FCSTD DOCUMENT  (FreeCAD 0.17R11204 (Git))
Label: Flow1D_thermomech
License: All rights reserved
LicenseURL: http://en.wikipedia.org/wiki/All_rights_reserved
objects: Fem::FeaturePython×12, Part::Part2DObjectPython×1, Fem::FemSolverObjectPython×1, Fem::FemMeshObjectPython×1, App::MaterialObjectPython×1, Fem::FemResultObjectPython×1, Fem::FemAnalysisPython×1
note: 1 computed .brp shape members not serialized (recipe doc carries the construction recipe); baked Part::Feature solids carry a one-line shape summary decoded from their .brp

FEATURE [Part::Part2DObjectPython] DWire  # Draft 2D object (typed FeaturePython)
  ChamferSize = 0
  Closed = false
  End = (15047,-2e-12,-7847.97)
  FilletRadius = 0
  Length = 30059.3
  MakeFace = false
  Placement = pos=(0,0,0) rot=(1,0,0;1.5708rad)
  Points = (14) [(0,50,0),(0,-50,0),(0,-4300,0),(4950,-4300,0),(5000,-4300,0),(8535.53,-7835.53,0),(8569.88,-7870.88,0),(12105.4,-11406.4,0),(12140.8,-11441.8,0),+5 more]
  Start = (0,0,50)
  Subdivisions = 0
FEATURE [Fem::FemSolverObjectPython] CalculiX  # FEM object (typed FeaturePython)
  AnalysisType = 2
  EigenmodeHighLimit = 1000000
  EigenmodeLowLimit = 0
  EigenmodesCount = 10
  GeometricalNonlinearity = 0
  IterationsControlParameterCutb = 0.25,0.5,0.75,0.85,,,1.5,
  IterationsControlParameterIter = 4,8,9,200,10,400,,200,,
  IterationsControlParameterTimeUse = false
  IterationsThermoMechMaximum = 2000
  IterationsUserDefinedIncrementations = false
  IterationsUserDefinedTimeStepLength = 0.1, 1.0
  MaterialNonlinearity = 0
  MatrixSolverType = 0
  SolverType = FemSolverCalculix
  SplitInputWriter = false
  ThermoMechSteadyState = true
  TimeEnd = 1
  TimeInitialStep = 1
FEATURE [Fem::FemMeshObjectPython] DWire_Mesh  # FEM object (typed FeaturePython)
  Algorithm2D = 0
  Algorithm3D = 0
  CharacteristicLengthMax = 7000
  CharacteristicLengthMin = 7000
  ElementDimension = 1
  ElementOrder = 1
  HighOrderOptimize = false
  OptimizeNetgen = false
  OptimizeStd = true
  Part = -> DWire
  RecombineAll = false
FEATURE [App::MaterialObjectPython] FluidMaterial  # material (typed FeaturePython)
  Category = 1
  Material = Density=998.0 kg/m^3,Description=Standard distilled water properties at 20 Degrees Celsius and 1 atm,DynamicViscosity=1.003e-3 kg/m/s,+7 more (map truncated)
FEATURE [Fem::FeaturePython] FemConstraintSelfWeight  # FEM object (typed FeaturePython)
  Gravity_x = 0
  Gravity_y = 0
  Gravity_z = -1
FEATURE [Fem::FeaturePython] ElementFluid1D  # FEM object (typed FeaturePython)
  BendAngle = 0
  BendLossCoefficient = 0
  BendPipeArea = 20
  BendRadiusDiameter = 1
  ChannelSectionType = 0
  ColebrookeArea = 20
  ColebrookeFormFactor = 1
  ColebrookeGrainDiameter = 0.0025
  ColebrookeRadius = 1
  ContractArea1 = 20
  ContractArea2 = 10
  DiaphragmArea = 20
  DiaphragmPipeArea = 20
  EnlargeArea1 = 10
  EnlargeArea2 = 20
  EntranceArea = 20
  EntrancePipeArea = 20
  GasSectionType = 0
  GateValveClosingCoeff = 0.125
  GateValvePipeArea = 20
  InletFlowRate = 1
  InletFlowRateActive = false
  InletPressure = 0.1
  InletPressureActive = true
  LiquidSectionType = 3
  ManningArea = 10
  ManningCoefficient = 0.002
  ManningRadius = 1
  OutletFlowRate = 1
  OutletFlowRateActive = false
  OutletPressure = 1
  OutletPressureActive = true
  PumpFlowRate = [0,0.000104,0.000208,0.000313,0.000417]
  PumpHeadLoss = [30,29.17,26.67,23.33,18.33]
  References = -> [DWire]
  SectionType = 0
FEATURE [Fem::FeaturePython] ElementFluid1D001  # FEM object (typed FeaturePython)
  BendAngle = 0
  BendLossCoefficient = 0
  BendPipeArea = 20
  BendRadiusDiameter = 1
  ChannelSectionType = 0
  ColebrookeArea = 20
  ColebrookeFormFactor = 1
  ColebrookeGrainDiameter = 0.0025
  ColebrookeRadius = 1
  ContractArea1 = 20
  ContractArea2 = 10
  DiaphragmArea = 20
  DiaphragmPipeArea = 20
  EnlargeArea1 = 10
  EnlargeArea2 = 20
  EntranceArea = 25133
  EntrancePipeArea = 31416
  GasSectionType = 0
  GateValveClosingCoeff = 0.125
  GateValvePipeArea = 20
  InletFlowRate = 1
  InletFlowRateActive = false
  InletPressure = 1
  InletPressureActive = true
  LiquidSectionType = 5
  ManningArea = 10
  ManningCoefficient = 0.002
  ManningRadius = 1
  OutletFlowRate = 1
  OutletFlowRateActive = false
  OutletPressure = 1
  OutletPressureActive = true
  PumpFlowRate = [0,0.000104,0.000208,0.000313,0.000417]
  PumpHeadLoss = [30,29.17,26.67,23.33,18.33]
  References = -> [DWire]
  SectionType = 0
FEATURE [Fem::FeaturePython] ElementFluid1D002  # FEM object (typed FeaturePython)
  BendAngle = 0
  BendLossCoefficient = 0
  BendPipeArea = 20
  BendRadiusDiameter = 1
  ChannelSectionType = 0
  ColebrookeArea = 20
  ColebrookeFormFactor = 1
  ColebrookeGrainDiameter = 0.0025
  ColebrookeRadius = 1
  ContractArea1 = 20
  ContractArea2 = 10
  DiaphragmArea = 20
  DiaphragmPipeArea = 20
  EnlargeArea1 = 10
  EnlargeArea2 = 20
  EntranceArea = 20
  EntrancePipeArea = 20
  GasSectionType = 0
  GateValveClosingCoeff = 0.125
  GateValvePipeArea = 20
  InletFlowRate = 1
  InletFlowRateActive = false
  InletPressure = 1
  InletPressureActive = true
  LiquidSectionType = 0
  ManningArea = 31416
  ManningCoefficient = 0.002
  ManningRadius = 50
  OutletFlowRate = 1
  OutletFlowRateActive = false
  OutletPressure = 1
  OutletPressureActive = true
  PumpFlowRate = [0,0.000104,0.000208,0.000313,0.000417]
  PumpHeadLoss = [30,29.17,26.67,23.33,18.33]
  References = -> [DWire]
  SectionType = 0
FEATURE [Fem::FeaturePython] ElementFluid1D003  # FEM object (typed FeaturePython)
  BendAngle = 45
  BendLossCoefficient = 0.4
  BendPipeArea = 31416
  BendRadiusDiameter = 1.5
  ChannelSectionType = 0
  ColebrookeArea = 20
  ColebrookeFormFactor = 1
  ColebrookeGrainDiameter = 0.0025
  ColebrookeRadius = 1
  ContractArea1 = 20
  ContractArea2 = 10
  DiaphragmArea = 20
  DiaphragmPipeArea = 20
  EnlargeArea1 = 10
  EnlargeArea2 = 20
  EntranceArea = 20
  EntrancePipeArea = 20
  GasSectionType = 0
  GateValveClosingCoeff = 0.125
  GateValvePipeArea = 20
  InletFlowRate = 1
  InletFlowRateActive = false
  InletPressure = 1
  InletPressureActive = true
  LiquidSectionType = 7
  ManningArea = 10
  ManningCoefficient = 0.002
  ManningRadius = 1
  OutletFlowRate = 1
  OutletFlowRateActive = false
  OutletPressure = 1
  OutletPressureActive = true
  PumpFlowRate = [0,0.000104,0.000208,0.000313,0.000417]
  PumpHeadLoss = [30,29.17,26.67,23.33,18.33]
  References = -> [DWire]
  SectionType = 0
FEATURE [Fem::FeaturePython] ElementFluid1D004  # FEM object (typed FeaturePython)
  BendAngle = 0
  BendLossCoefficient = 0
  BendPipeArea = 20
  BendRadiusDiameter = 1
  ChannelSectionType = 0
  ColebrookeArea = 20
  ColebrookeFormFactor = 1
  ColebrookeGrainDiameter = 0.0025
  ColebrookeRadius = 1
  ContractArea1 = 20
  ContractArea2 = 10
  DiaphragmArea = 20
  DiaphragmPipeArea = 20
  EnlargeArea1 = 31416
  EnlargeArea2 = 70686
  EntranceArea = 20
  EntrancePipeArea = 20
  GasSectionType = 0
  GateValveClosingCoeff = 0.125
  GateValvePipeArea = 20
  InletFlowRate = 1
  InletFlowRateActive = false
  InletPressure = 1
  InletPressureActive = true
  LiquidSectionType = 1
  ManningArea = 10
  ManningCoefficient = 0.002
  ManningRadius = 1
  OutletFlowRate = 1
  OutletFlowRateActive = false
  OutletPressure = 1
  OutletPressureActive = true
  PumpFlowRate = [0,0.000104,0.000208,0.000313,0.000417]
  PumpHeadLoss = [30,29.17,26.67,23.33,18.33]
  References = -> [DWire]
  SectionType = 0
FEATURE [Fem::FeaturePython] ElementFluid1D005  # FEM object (typed FeaturePython)
  BendAngle = 0
  BendLossCoefficient = 0
  BendPipeArea = 20
  BendRadiusDiameter = 1
  ChannelSectionType = 0
  ColebrookeArea = 20
  ColebrookeFormFactor = 1
  ColebrookeGrainDiameter = 0.0025
  ColebrookeRadius = 1
  ContractArea1 = 20
  ContractArea2 = 10
  DiaphragmArea = 20
  DiaphragmPipeArea = 20
  EnlargeArea1 = 10
  EnlargeArea2 = 20
  EntranceArea = 20
  EntrancePipeArea = 20
  GasSectionType = 0
  GateValveClosingCoeff = 0.125
  GateValvePipeArea = 20
  InletFlowRate = 1
  InletFlowRateActive = false
  InletPressure = 1
  InletPressureActive = true
  LiquidSectionType = 0
  ManningArea = 70686
  ManningCoefficient = 0.002
  ManningRadius = 75
  OutletFlowRate = 1
  OutletFlowRateActive = false
  OutletPressure = 1
  OutletPressureActive = true
  PumpFlowRate = [0,0.000104,0.000208,0.000313,0.000417]
  PumpHeadLoss = [30,29.17,26.67,23.33,18.33]
  References = -> [DWire]
  SectionType = 0
FEATURE [Fem::FeaturePython] ElementFluid1D006  # FEM object (typed FeaturePython)
  BendAngle = 0
  BendLossCoefficient = 0
  BendPipeArea = 20
  BendRadiusDiameter = 1
  ChannelSectionType = 0
  ColebrookeArea = 20
  ColebrookeFormFactor = 1
  ColebrookeGrainDiameter = 0.0025
  ColebrookeRadius = 1
  ContractArea1 = 70686
  ContractArea2 = 17671
  DiaphragmArea = 20
  DiaphragmPipeArea = 20
  EnlargeArea1 = 10
  EnlargeArea2 = 20
  EntranceArea = 20
  EntrancePipeArea = 20
  GasSectionType = 0
  GateValveClosingCoeff = 0.125
  GateValvePipeArea = 20
  InletFlowRate = 1
  InletFlowRateActive = false
  InletPressure = 1
  InletPressureActive = true
  LiquidSectionType = 2
  ManningArea = 10
  ManningCoefficient = 0.002
  ManningRadius = 1
  OutletFlowRate = 1
  OutletFlowRateActive = false
  OutletPressure = 1
  OutletPressureActive = true
  PumpFlowRate = [0,0.000104,0.000208,0.000313,0.000417]
  PumpHeadLoss = [30,29.17,26.67,23.33,18.33]
  References = -> [DWire]
  SectionType = 0
FEATURE [Fem::FeaturePython] ElementFluid1D007  # FEM object (typed FeaturePython)
  BendAngle = 0
  BendLossCoefficient = 0
  BendPipeArea = 20
  BendRadiusDiameter = 1
  ChannelSectionType = 0
  ColebrookeArea = 20
  ColebrookeFormFactor = 1
  ColebrookeGrainDiameter = 0.0025
  ColebrookeRadius = 1
  ContractArea1 = 20
  ContractArea2 = 10
  DiaphragmArea = 20
  DiaphragmPipeArea = 20
  EnlargeArea1 = 10
  EnlargeArea2 = 20
  EntranceArea = 20
  EntrancePipeArea = 20
  GasSectionType = 0
  GateValveClosingCoeff = 0.125
  GateValvePipeArea = 20
  InletFlowRate = 1
  InletFlowRateActive = false
  InletPressure = 1
  InletPressureActive = true
  LiquidSectionType = 0
  ManningArea = 17671
  ManningCoefficient = 0.002
  ManningRadius = 37.5
  OutletFlowRate = 1
  OutletFlowRateActive = false
  OutletPressure = 1
  OutletPressureActive = true
  PumpFlowRate = [0,0.000104,0.000208,0.000313,0.000417]
  PumpHeadLoss = [30,29.17,26.67,23.33,18.33]
  References = -> [DWire]
  SectionType = 0
FEATURE [Fem::FeaturePython] ElementFluid1D008  # FEM object (typed FeaturePython)
  BendAngle = 0
  BendLossCoefficient = 0
  BendPipeArea = 20
  BendRadiusDiameter = 1
  ChannelSectionType = 0
  ColebrookeArea = 20
  ColebrookeFormFactor = 1
  ColebrookeGrainDiameter = 0.0025
  ColebrookeRadius = 1
  ContractArea1 = 20
  ContractArea2 = 10
  DiaphragmArea = 20
  DiaphragmPipeArea = 20
  EnlargeArea1 = 10
  EnlargeArea2 = 20
  EntranceArea = 20
  EntrancePipeArea = 20
  GasSectionType = 0
  GateValveClosingCoeff = 0.5
  GateValvePipeArea = 17661
  InletFlowRate = 1
  InletFlowRateActive = false
  InletPressure = 1
  InletPressureActive = true
  LiquidSectionType = 8
  ManningArea = 10
  ManningCoefficient = 0.002
  ManningRadius = 1
  OutletFlowRate = 1
  OutletFlowRateActive = false
  OutletPressure = 1
  OutletPressureActive = true
  PumpFlowRate = [0,0.000104,0.000208,0.000313,0.000417]
  PumpHeadLoss = [30,29.17,26.67,23.33,18.33]
  References = -> [DWire]
  SectionType = 0
FEATURE [Fem::FeaturePython] ElementFluid1D009  # FEM object (typed FeaturePython)
  BendAngle = 0
  BendLossCoefficient = 0
  BendPipeArea = 20
  BendRadiusDiameter = 1
  ChannelSectionType = 0
  ColebrookeArea = 20
  ColebrookeFormFactor = 1
  ColebrookeGrainDiameter = 0.0025
  ColebrookeRadius = 1
  ContractArea1 = 20
  ContractArea2 = 10
  DiaphragmArea = 20
  DiaphragmPipeArea = 20
  EnlargeArea1 = 17671
  EnlargeArea2 = 1000000000000
  EntranceArea = 20
  EntrancePipeArea = 20
  GasSectionType = 0
  GateValveClosingCoeff = 0.125
  GateValvePipeArea = 20
  InletFlowRate = 1
  InletFlowRateActive = false
  InletPressure = 1
  InletPressureActive = true
  LiquidSectionType = 1
  ManningArea = 10
  ManningCoefficient = 0.002
  ManningRadius = 1
  OutletFlowRate = 1
  OutletFlowRateActive = false
  OutletPressure = 1
  OutletPressureActive = true
  PumpFlowRate = [0,0.000104,0.000208,0.000313,0.000417]
  PumpHeadLoss = [30,29.17,26.67,23.33,18.33]
  References = -> [DWire]
  SectionType = 0
FEATURE [Fem::FeaturePython] ElementFluid1D010  # FEM object (typed FeaturePython)
  BendAngle = 0
  BendLossCoefficient = 0
  BendPipeArea = 20
  BendRadiusDiameter = 1
  ChannelSectionType = 0
  ColebrookeArea = 20
  ColebrookeFormFactor = 1
  ColebrookeGrainDiameter = 0.0025
  ColebrookeRadius = 1
  ContractArea1 = 20
  ContractArea2 = 10
  DiaphragmArea = 20
  DiaphragmPipeArea = 20
  EnlargeArea1 = 10
  EnlargeArea2 = 20
  EntranceArea = 20
  EntrancePipeArea = 20
  GasSectionType = 0
  GateValveClosingCoeff = 0.125
  GateValvePipeArea = 20
  InletFlowRate = 1
  InletFlowRateActive = false
  InletPressure = 1
  InletPressureActive = true
  LiquidSectionType = 4
  ManningArea = 10
  ManningCoefficient = 0.002
  ManningRadius = 1
  OutletFlowRate = 1
  OutletFlowRateActive = false
  OutletPressure = 0.1
  OutletPressureActive = true
  PumpFlowRate = [0,0.000104,0.000208,0.000313,0.000417]
  PumpHeadLoss = [30,29.17,26.67,23.33,18.33]
  References = -> [DWire]
  SectionType = 0
FEATURE [Fem::FemResultObjectPython] CalculiX_thermomech_results  # FEM object (typed FeaturePython)
  Eigenmode = 0
  EigenmodeFrequency = 0
  MassFlowRate = [78.5376,78.5376,78.5376,78.5376,78.5376,78.5376,78.5376,78.5376,78.5376,78.5376,78.5376,78.5376,78.5376,78.5376,78.5376,78.5376,78.5376,78.5376,78.5376,78.5376,78.5376,78.5376,78.5376,78.5376,78.5376,78.5376,78.5376]
  Mesh = -> DWire_Mesh
  NetworkPressure = [0.1,0.1,0.134912,0.128322,0.128009,0.156036,0.157918,0.191836,0.179121,0.181025,0.161596,0.162784,0.1,0.1,0.1,0.117456,0.131617,0.128165,0.142023,0.156977,0.174877,0.185478,0.180073,0.17131,0.16219,0.131392,0.1]
  NodeNumbers = [0]
  ResultType = FemResultMechanical
  Stats = [0,0,0,0,0,0,0,0,0,0,0,0,0,0,0,0,0,0,0,0,0,0,0,0,0,0,0,0,0,0]
  Time = 1
FEATURE [Fem::FemAnalysisPython] Analysis  # FEM object (typed FeaturePython)
  Member = -> [CalculiX,DWire_Mesh,FluidMaterial,FemConstraintSelfWeight,ElementFluid1D,ElementFluid1D001,ElementFluid1D002,ElementFluid1D003,ElementFluid1D004,ElementFluid1D005,ElementFluid1D006,ElementFluid1D007,ElementFluid1D008,ElementFluid1D009,ElementFluid1D010,CalculiX_thermomech_results]
